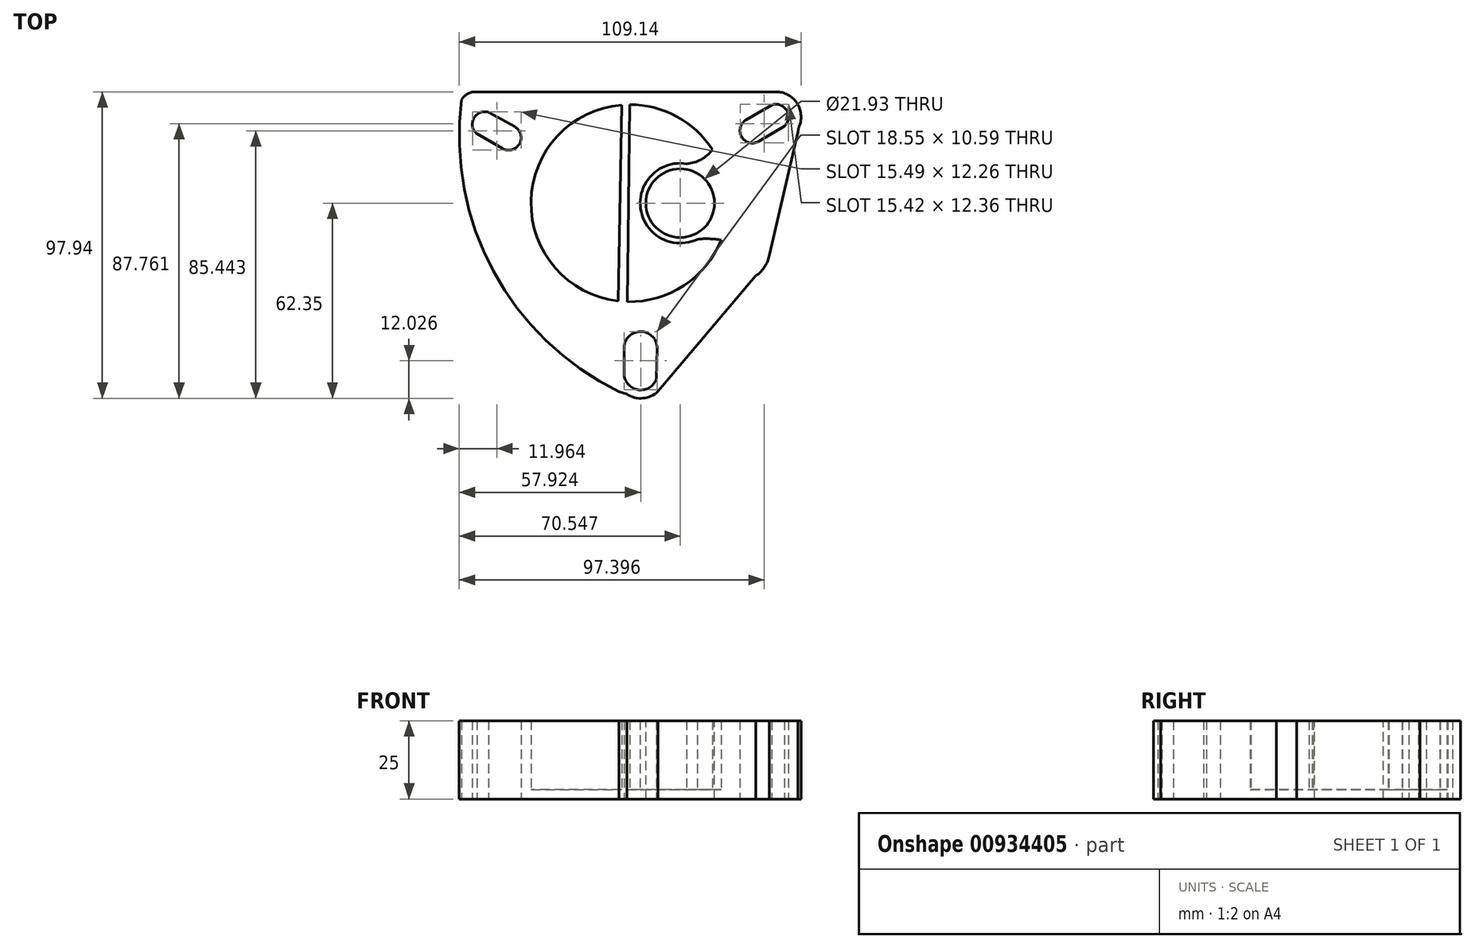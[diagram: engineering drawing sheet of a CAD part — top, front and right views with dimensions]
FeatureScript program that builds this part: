
annotation { "Feature Type Name" : "Feature", "Feature Type Description" : "" }
export const myFeature = defineFeature(function(context is Context, id is Id, definition is map)
    precondition{}
    {
        {
            var Q0;
            Q0=qCreatedBy(makeId("Top.planeOp"),FACE);
            var sketch = newSketch(context, id + "F0", { "sketchPlane" : qUnion([Q0])});
            skCircle(sketch, "E0", {"center": v(0, 0) * mm, "radius": 31.5 * mm});
            skArc(sketch, "E1", {"start": v(37.22, 26.65) * mm, "mid": v(35.78, 21.16) * mm, "end": v(41.29, 19.76) * mm});
            skPoint(sketch, "E2.center", {"position": v(0.92, -0.43) * mm});
            skArc(sketch, "E3", {"start": v(49.45, 24.66) * mm, "mid": v(50.13, 29.69) * mm, "end": v(45.34, 31.34) * mm});
            skLineSegment(sketch, "E4", {"start": v(45.34, 31.34) * mm, "end": v(37.22, 26.65) * mm});
            skLineSegment(sketch, "E5", {"start": v(49.45, 24.66) * mm, "end": v(41.17, 19.7) * mm});
            skArc(sketch, "E6.1.0", {"start": v(-45.07, 29.05) * mm, "mid": v(-49.76, 27.13) * mm, "end": v(-48.8, 22.15) * mm});
            skLineSegment(sketch, "E6.1.1", {"start": v(-48.8, 22.15) * mm, "end": v(-40.68, 17.47) * mm});
            skArc(sketch, "E6.1.2", {"start": v(-40.68, 17.47) * mm, "mid": v(-35.2, 18.96) * mm, "end": v(-36.74, 24.43) * mm});
            skLineSegment(sketch, "E6.1.3", {"start": v(-45.07, 29.05) * mm, "end": v(-36.63, 24.37) * mm});
            skArc(sketch, "E6.2.0", {"start": v(-1.79, -54.35) * mm, "mid": v(2.65, -59.6) * mm, "end": v(8.56, -56.1) * mm});
            skLineSegment(sketch, "E6.2.1", {"start": v(8.56, -56.1) * mm, "end": v(8.8, -46.35) * mm});
            skArc(sketch, "E6.2.2", {"start": v(8.8, -46.35) * mm, "mid": v(3.9, -41.05) * mm, "end": v(-1.78, -45.48) * mm});
            skArc(sketch, "E7", {"start": v(54.15, 24.6) * mm, "mid": v(53.35, 32.07) * mm, "end": v(46.72, 35.6) * mm});
            skArc(sketch, "E8", {"start": v(-0.92, -61) * mm, "mid": v(4.23, -62.32) * mm, "end": v(9.06, -60.13) * mm});
            skLineSegment(sketch, "E9", {"start": v(46.72, 35.6) * mm, "end": v(-49.3, 35.6) * mm});
            skPoint(sketch, "E10.endSnap0", {"position": v(-1.87, -49.52) * mm});
            skPoint(sketch, "E11.orphan", {"position": v(-1.96, -44.7) * mm});
            skLineSegment(sketch, "E12", {"start": v(-1.78, -45.48) * mm, "end": v(-1.79, -54.35) * mm});
            skPoint(sketch, "E13.visualSharp", {"position": v(-52.14, 35.6) * mm});
            skArc(sketch, "E13.filletArc", {"start": v(-49.3, 35.6) * mm, "mid": v(-51.82, 34.91) * mm, "end": v(-53.66, 33.05) * mm});
            skPoint(sketch, "E14.visualSharp", {"position": v(53.79, 23.83) * mm});
            skArc(sketch, "E14.filletArc", {"start": v(54.15, 24.6) * mm, "mid": v(53.88, 23.7) * mm, "end": v(53.79, 22.75) * mm});
            skPoint(sketch, "E15.visualSharp", {"position": v(43.85, -20.83) * mm});
            skArc(sketch, "E15.filletArc", {"start": v(40.3, -23.2) * mm, "mid": v(43.12, -20.35) * mm, "end": v(44.6, -16.62) * mm});
            skLineSegment(sketch, "E16", {"start": v(53.79, 22.75) * mm, "end": v(44.6, -16.62) * mm});
            skLineSegment(sketch, "E17", {"start": v(40.3, -23.2) * mm, "end": v(9.06, -60.13) * mm});
            skArc(sketch, "E18", {"start": v(-53.66, 33.05) * mm, "mid": v(-43.55, -21.67) * mm, "end": v(-3.36, -60.16) * mm});
            skLineSegment(sketch, "E19", {"start": v(-0.92, -61) * mm, "end": v(-3.36, -60.16) * mm});
            skLineSegment(sketch, "E20", {"start": v(-0.71, -31.5) * mm, "end": v(0, 31.5) * mm});
            skLineSegment(sketch, "E21", {"start": v(-2.57, 31.4) * mm, "end": v(-3.7, -31.28) * mm});
            skSolve(sketch);
        }
        {
            var Q0;
            Q0=makeQuery(id+"F0.imprint","IMPRINT",FACE,{"disambiguationData":[TD([[makeQuery(id+"F0.imprint","IMPRINT",EDGE,{"derivedFrom":sQuery(id+"F0.wireOp",EDGE,"E0")}),-1.0]])]});
            extrude(context, id + "F1", {"entities" : qUnion([Q0]), "depth" : 25 * mm, "offsetDistance" : 25 * mm});
        }
        {
            var Q0;
            Q0=makeQuery(id+"F1.opExtrude","CAP_FACE",FACE,{"disambiguationData":[OSD([sQuery(id+"F0.wireOp",EDGE,"E0"),sQuery(id+"F0.wireOp",EDGE,"E1"),sQuery(id+"F0.wireOp",EDGE,"E3"),sQuery(id+"F0.wireOp",EDGE,"E4"),sQuery(id+"F0.wireOp",EDGE,"E5"),sQuery(id+"F0.wireOp",EDGE,"E6.1.0"),sQuery(id+"F0.wireOp",EDGE,"E6.1.1"),sQuery(id+"F0.wireOp",EDGE,"E6.1.2"),sQuery(id+"F0.wireOp",EDGE,"E6.1.3"),sQuery(id+"F0.wireOp",EDGE,"E6.2.0"),sQuery(id+"F0.wireOp",EDGE,"E6.2.1"),sQuery(id+"F0.wireOp",EDGE,"E6.2.2"),sQuery(id+"F0.wireOp",EDGE,"E7"),sQuery(id+"F0.wireOp",EDGE,"E8"),sQuery(id+"F0.wireOp",EDGE,"E9"),sQuery(id+"F0.wireOp",EDGE,"E12"),sQuery(id+"F0.wireOp",EDGE,"E13.filletArc"),sQuery(id+"F0.wireOp",EDGE,"E14.filletArc"),sQuery(id+"F0.wireOp",EDGE,"E15.filletArc"),sQuery(id+"F0.wireOp",EDGE,"E16"),sQuery(id+"F0.wireOp",EDGE,"E17"),sQuery(id+"F0.wireOp",EDGE,"E18"),sQuery(id+"F0.wireOp",EDGE,"E19")])],"isStart":true});
            var sketch = newSketch(context, id + "F2", { "sketchPlane" : qUnion([Q0])});
            skCircle(sketch, "E22", {"center": v(0, 0) * mm, "radius": 33.5 * mm});
            skSolve(sketch);
        }
        {
            var Q0;
            Q0=makeQuery(id+"F2.imprint","IMPRINT",FACE,{"disambiguationData":[TD([[makeQuery(id+"F2.imprint","IMPRINT",EDGE,{"derivedFrom":makeQuery(id+"F1.opExtrude","CAP_EDGE",EDGE,{"disambiguationData":[OSD([sQuery(id+"F0.wireOp",EDGE,"E0")])],"isStart":true})}),-1.0]])]});
            extrude(context, id + "F3", {"entities" : qUnion([Q0]), "operationType" : NewBodyOperationType.ADD, "oppositeDirection" : true, "depth" : 3 * mm, "offsetDistance" : 25 * mm});
        }
        {
            var Q0;
            Q0=makeQuery(id+"F3.opExtrude","CAP_FACE",FACE,{"disambiguationData":[OSD([sQuery(id+"F0.wireOp",EDGE,"E0")])],"isStart":false});
            var sketch = newSketch(context, id + "F4", { "sketchPlane" : qUnion([Q0])});
            skCircle(sketch, "E23", {"center": v(16.13, 0) * mm, "radius": 10.97 * mm});
            skArc(sketch, "E24", {"start": v(18.23, 12.6) * mm, "mid": v(3.49, -1.78) * mm, "end": v(21.63, -11.52) * mm});
            skArc(sketch, "E25", {"start": v(18.23, 12.6) * mm, "mid": v(22.82, 13.98) * mm, "end": v(26.43, 17.13) * mm});
            skArc(sketch, "E26", {"start": v(29.23, -11.73) * mm, "mid": v(25.44, -11.38) * mm, "end": v(21.63, -11.52) * mm});
            skArc(sketch, "E27", {"start": v(29.23, -11.73) * mm, "mid": v(32.59, 3.16) * mm, "end": v(26.43, 17.13) * mm});
            skSolve(sketch);
        }
        {
            var Q0;
            Q0=makeQuery(id+"F4.imprint","IMPRINT",FACE,{"disambiguationData":[TD([[makeQuery(id+"F4.imprint","IMPRINT",EDGE,{"derivedFrom":sQuery(id+"F4.wireOp",EDGE,"E23")}),1.0]])]});
            extrude(context, id + "F5", {"entities" : qUnion([Q0]), "operationType" : NewBodyOperationType.REMOVE, "oppositeDirection" : true, "depth" : 25 * mm, "offsetDistance" : 25 * mm});
        }
        {
            var Q0;
            Q0 = qSketchRegion(id + "F4", true);
            extrude(context, id + "F6", {"entities" : qUnion([Q0]), "operationType" : NewBodyOperationType.ADD, "depth" : 22 * mm, "offsetDistance" : 25 * mm});
        }
        {
            var Q0;
            {var subQ0=sQuery(id+"F0.wireOp",EDGE,"E20");Q0=makeQuery(id+"F0.imprint","IMPRINT",FACE,{"disambiguationData":[TD([[makeQuery(id+"F0.imprint","IMPRINT",EDGE,{"derivedFrom":subQ0}),1.0]])]});}
            extrude(context, id + "F7", {"entities" : qUnion([Q0]), "operationType" : NewBodyOperationType.ADD, "depth" : 25 * mm, "offsetDistance" : 25 * mm});
        }
    });
